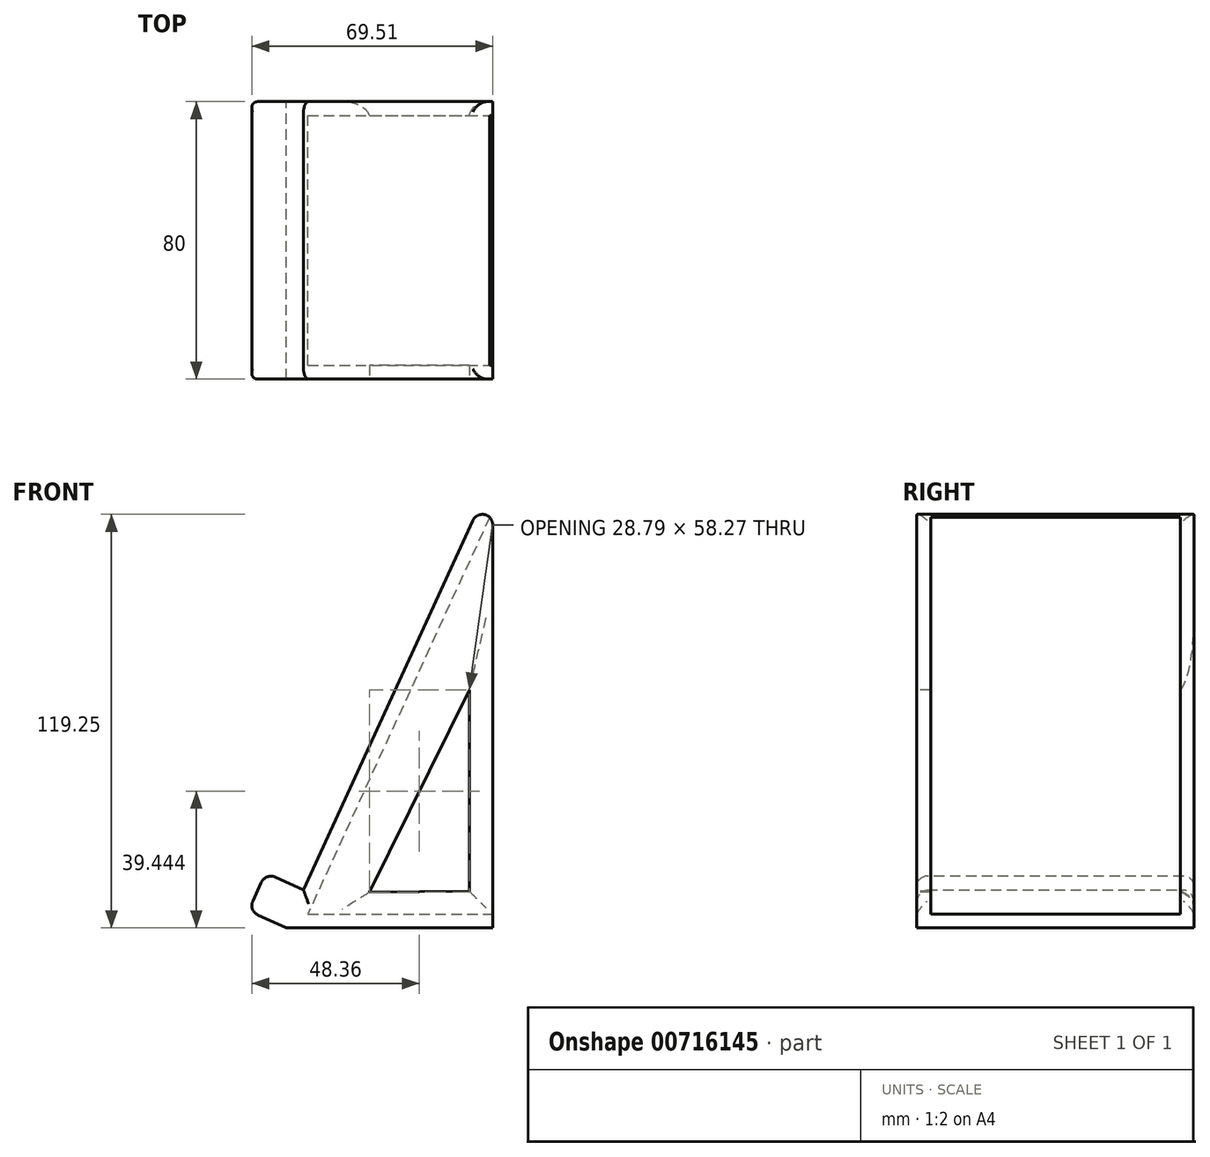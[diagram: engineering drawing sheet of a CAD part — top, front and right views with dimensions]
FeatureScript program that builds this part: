
annotation { "Feature Type Name" : "Feature", "Feature Type Description" : "" }
export const myFeature = defineFeature(function(context is Context, id is Id, definition is map)
    precondition{}
    {
        {
            var Q0;
            Q0=qCreatedBy(makeId("Front.planeOp"),FACE);
            var sketch = newSketch(context, id + "F0", { "sketchPlane" : qUnion([Q0])});
            skLineSegment(sketch, "E0", {"start": v(0, 0) * mm, "end": v(0, 130) * mm});
            skLineSegment(sketch, "E1", {"start": v(0, 130) * mm, "end": v(-59.58, 0) * mm});
            skLineSegment(sketch, "E2", {"start": v(-59.58, 0) * mm, "end": v(0, 0) * mm});
            skSolve(sketch);
        }
        {
            var Q0;
            Q0 = qSketchRegion(id + "F0", true);
            extrude(context, id + "F1", {"entities" : qUnion([Q0]), "depth" : 80 * mm, "offsetDistance" : 25 * mm});
        }
        {
            var Q0;
            Q0=makeQuery(id+"F1.opExtrude","SWEPT_FACE",FACE,{"disambiguationData":[OSD([sQuery(id+"F0.wireOp",EDGE,"E0")])]});
            shell(context, id + "F2", {"entities" : qUnion([Q0]), "thickness" : 4 * mm});
        }
        {
            var Q0;
            Q0=makeQuery(id+"F1.opExtrude","CAP_FACE",FACE,{"disambiguationData":[OSD([sQuery(id+"F0.wireOp",EDGE,"E0"),sQuery(id+"F0.wireOp",EDGE,"E1"),sQuery(id+"F0.wireOp",EDGE,"E2")])],"isStart":false});
            var sketch = newSketch(context, id + "F3", { "sketchPlane" : qUnion([Q0])});
            skLineSegment(sketch, "E3", {"start": v(-6.75, 10.58) * mm, "end": v(-6.75, 68.58) * mm});
            skLineSegment(sketch, "E4", {"start": v(-6.75, 68.58) * mm, "end": v(-35.55, 10.3) * mm});
            skLineSegment(sketch, "E5", {"start": v(-35.55, 10.3) * mm, "end": v(-6.75, 10.58) * mm});
            skSolve(sketch);
        }
        {
            var Q0;
            Q0=makeQuery(id+"F3.imprint","IMPRINT",FACE,{"disambiguationData":[TD([[makeQuery(id+"F3.imprint","IMPRINT",EDGE,{"derivedFrom":sQuery(id+"F3.wireOp",EDGE,"E3")}),1.0]])]});
            extrude(context, id + "F4", {"entities" : qUnion([Q0]), "operationType" : NewBodyOperationType.REMOVE, "endBound" : BoundingType.THROUGH_ALL, "oppositeDirection" : true, "depth" : 25 * mm, "offsetDistance" : 25 * mm});
        }
        {
            var Q0;
            Q0=makeQuery(id+"F1.opExtrude","SWEPT_FACE",FACE,{"disambiguationData":[OSD([sQuery(id+"F0.wireOp",EDGE,"E1")])]});
            var sketch = newSketch(context, id + "F5", { "sketchPlane" : qUnion([Q0])});
            skLineSegment(sketch, "E6.bottom", {"start": v(80, -24.82) * mm, "end": v(0, -24.82) * mm});
            skLineSegment(sketch, "E6.top", {"start": v(80, -12.82) * mm, "end": v(0, -12.82) * mm});
            skLineSegment(sketch, "E6.left", {"start": v(80, -24.82) * mm, "end": v(80, -12.82) * mm});
            skLineSegment(sketch, "E6.right", {"start": v(0, -24.82) * mm, "end": v(0, -12.82) * mm});
            skSolve(sketch);
        }
        {
            var Q0;
            Q0 = qSketchRegion(id + "F5", true);
            extrude(context, id + "F6", {"entities" : qUnion([Q0]), "operationType" : NewBodyOperationType.ADD, "depth" : 12 * mm, "offsetDistance" : 25 * mm});
        }
        {
            var Q0;
            Q0=makeQuery(id+"F1.opExtrude","SWEPT_EDGE",EDGE,{"disambiguationData":[OSD([sQuery(id+"F0.wireOp",EDGE,"E0"),sQuery(id+"F0.wireOp",EDGE,"E1")])]});
            var Q1;
            Q1=makeQuery(id+"F1.opExtrude","CAP_EDGE",EDGE,{"disambiguationData":[OSD([sQuery(id+"F0.wireOp",EDGE,"E1")])],"isStart":true});
            var Q2;
            Q2=makeQuery(id+"F1.opExtrude","CAP_EDGE",EDGE,{"disambiguationData":[OSD([sQuery(id+"F0.wireOp",EDGE,"E1")])],"isStart":false});
            var Q3;
            Q3=makeQuery(id+"F6.opExtrude","SWEPT_EDGE",EDGE,{"disambiguationData":[OSD([sQuery(id+"F0.wireOp",EDGE,"E1"),sQuery(id+"F5.wireOp",EDGE,"E6.top"),sQuery(id+"F5.wireOp",EDGE,"E6.right")])]});
            var Q4;
            Q4=makeQuery(id+"F6.opExtrude","SWEPT_EDGE",EDGE,{"disambiguationData":[OSD([sQuery(id+"F0.wireOp",EDGE,"E1"),sQuery(id+"F5.wireOp",EDGE,"E6.top"),sQuery(id+"F5.wireOp",EDGE,"E6.left")])]});
            var Q5;
            Q5=makeQuery(id+"F6.opExtrude","CAP_EDGE",EDGE,{"disambiguationData":[OSD([sQuery(id+"F5.wireOp",EDGE,"E6.top")])],"isStart":false});
            var Q6;
            Q6=makeQuery(id+"F6.opExtrude","CAP_EDGE",EDGE,{"disambiguationData":[OSD([sQuery(id+"F5.wireOp",EDGE,"E6.bottom")])],"isStart":false});
            var Q7;
            Q7=makeQuery(id+"F6.opExtrude","CAP_EDGE",EDGE,{"disambiguationData":[OSD([sQuery(id+"F5.wireOp",EDGE,"E6.left")])],"isStart":false});
            var Q8;
            Q8=makeQuery(id+"F6.opExtrude","CAP_EDGE",EDGE,{"disambiguationData":[OSD([sQuery(id+"F5.wireOp",EDGE,"E6.right")])],"isStart":false});
            fillet(context, id + "F7", {"entities" : qUnion([Q0, Q1, Q2, Q3, Q4, Q5, Q6, Q7, Q8]), "radius" : 3 * mm, "tangentPropagation" : true, "allowEdgeOverflow" : false});
        }
        {
            var Q0;
            Q0=makeQuery(id+"F6.opExtrude","CAP_EDGE",EDGE,{"disambiguationData":[OSD([sQuery(id+"F5.wireOp",EDGE,"E6.top")])],"isStart":false});
            var Q1;
            Q1=makeQuery(id+"F6.opExtrude","CAP_EDGE",EDGE,{"disambiguationData":[OSD([sQuery(id+"F5.wireOp",EDGE,"E6.bottom")])],"isStart":false});
            var Q2;
            Q2=makeQuery(id+"F4.boolean.opBoolean","COPY",EDGE,{"derivedFrom":makeQuery(id+"F4.opExtrude","CAP_EDGE",EDGE,{"disambiguationData":[OSD([sQuery(id+"F3.wireOp",EDGE,"E4")])],"isStart":true})});
            var Q3;
            Q3=makeQuery(id+"F4.boolean.opBoolean","COPY",EDGE,{"derivedFrom":makeQuery(id+"F4.opExtrude","CAP_EDGE",EDGE,{"disambiguationData":[OSD([sQuery(id+"F3.wireOp",EDGE,"E3")])],"isStart":true})});
            var Q4;
            Q4=makeQuery(id+"F4.boolean.opBoolean","COPY",EDGE,{"derivedFrom":makeQuery(id+"F4.opExtrude","CAP_EDGE",EDGE,{"disambiguationData":[OSD([sQuery(id+"F3.wireOp",EDGE,"E5")])],"isStart":true})});
            var Q5;
            Q5=makeQuery(id+"F4.boolean.opBoolean","INTERSECT",EDGE,{"derivedFrom":[makeQuery(id+"F1.opExtrude","CAP_FACE",FACE,{"disambiguationData":[OSD([sQuery(id+"F0.wireOp",EDGE,"E0"),sQuery(id+"F0.wireOp",EDGE,"E1"),sQuery(id+"F0.wireOp",EDGE,"E2")])],"isStart":true}),makeQuery(id+"F4.opExtrude","SWEPT_FACE",FACE,{"disambiguationData":[OSD([sQuery(id+"F3.wireOp",EDGE,"E4")])]})]});
            var Q6;
            Q6=makeQuery(id+"F4.boolean.opBoolean","INTERSECT",EDGE,{"derivedFrom":[makeQuery(id+"F1.opExtrude","CAP_FACE",FACE,{"disambiguationData":[OSD([sQuery(id+"F0.wireOp",EDGE,"E0"),sQuery(id+"F0.wireOp",EDGE,"E1"),sQuery(id+"F0.wireOp",EDGE,"E2")])],"isStart":true}),makeQuery(id+"F4.opExtrude","SWEPT_FACE",FACE,{"disambiguationData":[OSD([sQuery(id+"F3.wireOp",EDGE,"E3")])]})]});
            var Q7;
            Q7=makeQuery(id+"F4.boolean.opBoolean","INTERSECT",EDGE,{"derivedFrom":[makeQuery(id+"F1.opExtrude","CAP_FACE",FACE,{"disambiguationData":[OSD([sQuery(id+"F0.wireOp",EDGE,"E0"),sQuery(id+"F0.wireOp",EDGE,"E1"),sQuery(id+"F0.wireOp",EDGE,"E2")])],"isStart":true}),makeQuery(id+"F4.opExtrude","SWEPT_FACE",FACE,{"disambiguationData":[OSD([sQuery(id+"F3.wireOp",EDGE,"E5")])]})]});
            fillet(context, id + "F8", {"entities" : qUnion([Q0, Q1, Q2, Q3, Q4, Q5, Q6, Q7]), "radius" : 5 * mm, "tangentPropagation" : true, "allowEdgeOverflow" : false});
        }
    });
